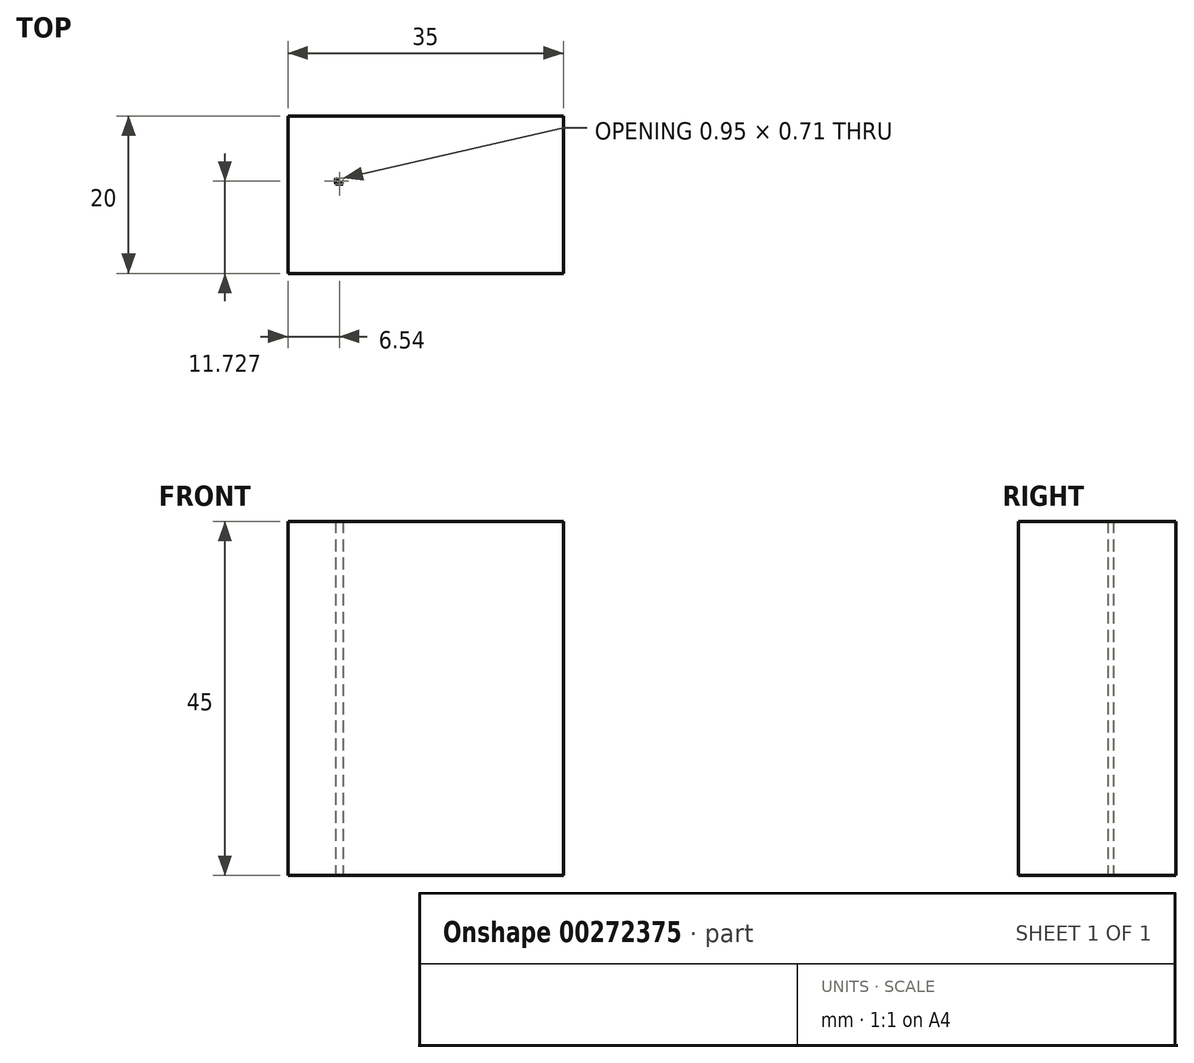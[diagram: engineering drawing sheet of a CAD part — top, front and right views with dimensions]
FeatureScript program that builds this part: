
annotation { "Feature Type Name" : "Feature", "Feature Type Description" : "" }
export const myFeature = defineFeature(function(context is Context, id is Id, definition is map)
    precondition{}
    {
        {
            var Q0;
            Q0=qCreatedBy(makeId("Top.planeOp"),FACE);
            var sketch = newSketch(context, id + "F0", { "sketchPlane" : qUnion([Q0])});
            skLineSegment(sketch, "E0.bottom", {"start": v(-17.5, 10) * mm, "end": v(17.5, 10) * mm});
            skLineSegment(sketch, "E0.top", {"start": v(-17.5, -10) * mm, "end": v(17.5, -10) * mm});
            skLineSegment(sketch, "E0.left", {"start": v(-17.5, 10) * mm, "end": v(-17.5, -10) * mm});
            skLineSegment(sketch, "E0.right", {"start": v(17.5, 10) * mm, "end": v(17.5, -10) * mm});
            skPoint(sketch, "E0.middle", {"position": v(0, 0) * mm});
            skLineSegment(sketch, "E1.bottom", {"start": v(-11.44, 2.08) * mm, "end": v(-10.48, 1.37) * mm});
            skLineSegment(sketch, "E1.top", {"start": v(-11.44, 1.37) * mm, "end": v(-10.48, 1.37) * mm});
            skLineSegment(sketch, "E1.left", {"start": v(-11.44, 2.08) * mm, "end": v(-11.44, 1.37) * mm});
            skLineSegment(sketch, "E1.right", {"start": v(-10.48, 1.37) * mm, "end": v(-10.48, 1.37) * mm});
            skSolve(sketch);
        }
        {
            var Q0;
            Q0=makeQuery(id+"F0.imprint","IMPRINT",FACE,{"disambiguationData":[TD([[makeQuery(id+"F0.imprint","IMPRINT",EDGE,{"derivedFrom":sQuery(id+"F0.wireOp",EDGE,"E0.bottom")}),-1.0]])]});
            extrude(context, id + "F1", {"entities" : qUnion([Q0]), "depth" : 45 * mm});
        }
    });
